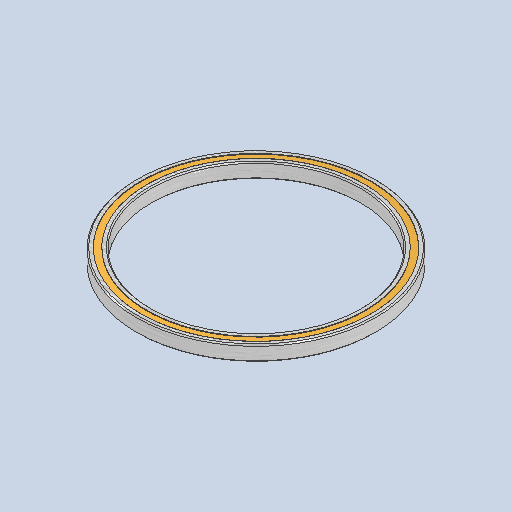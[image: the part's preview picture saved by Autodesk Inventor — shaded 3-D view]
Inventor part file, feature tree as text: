
AUTODESK INVENTOR PART (.ipt)
format: ipt  version: 2024 (Build 280153000, 153)  size: 165,376 bytes
history: native  units: in
note: dims shown in document units (in); Inventor stores cm internally (conversion verified against a paired STEP export)
features: revolve x1
ambient origin geometry x8: Origin, YZ Plane, XZ Plane, XY Plane, X Axis, Y Axis, Z Axis, Center Point
bodies: Solid1 (feature_tree)
feature tree (1):
  revolve  "Revolve1"  [1 undecoded]
note: 1 required parameter value undecoded (feature->parameter linkage not recoverable at this tier; creation-order binding heuristic only, values carry confidence <= 0.55)
